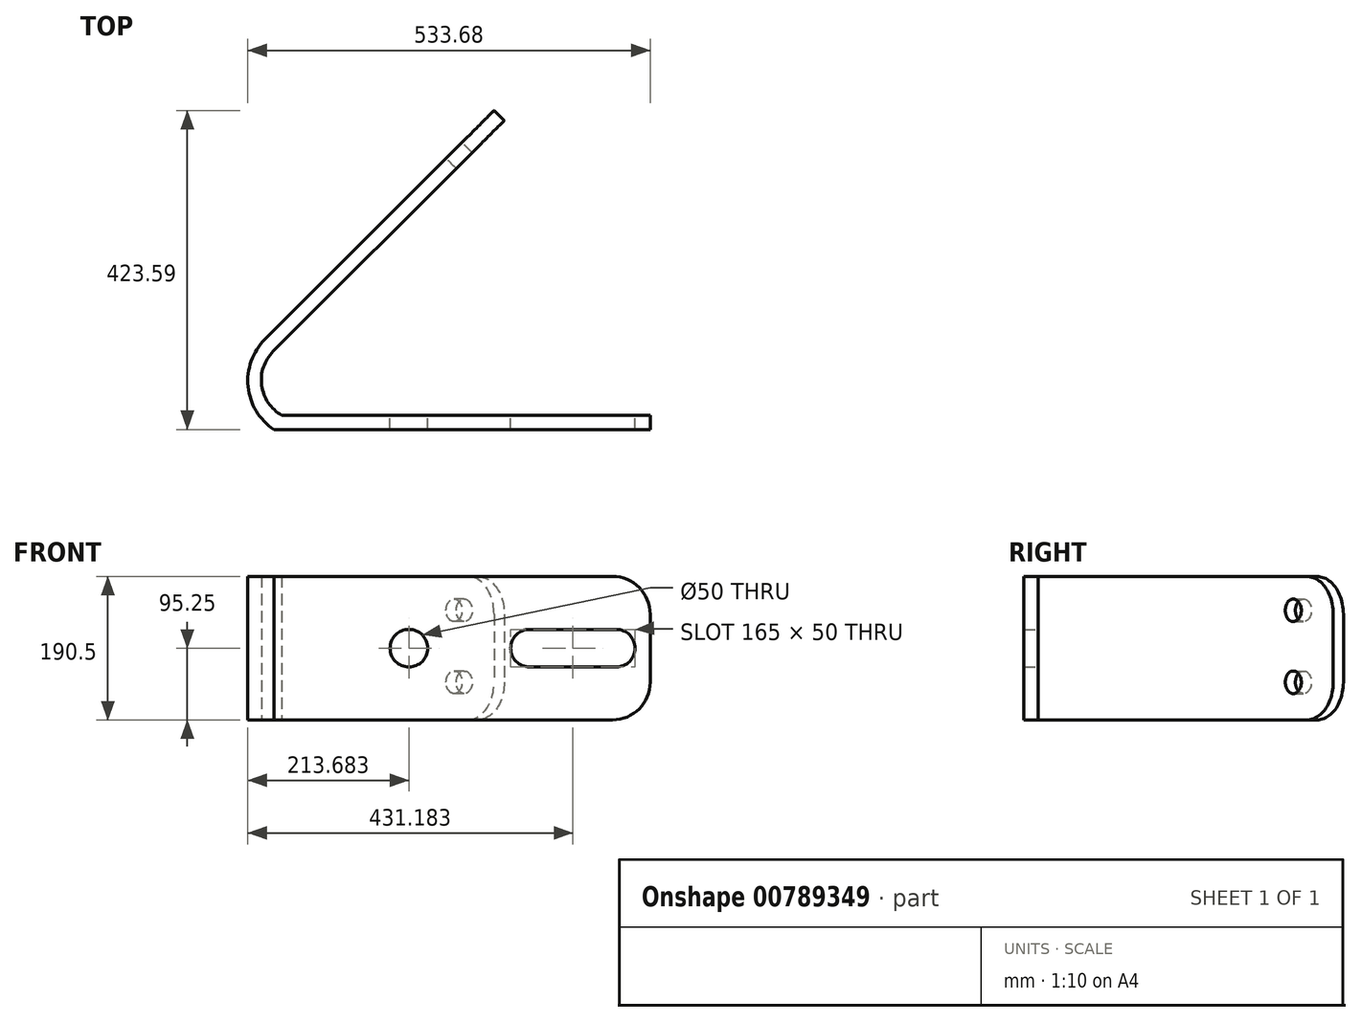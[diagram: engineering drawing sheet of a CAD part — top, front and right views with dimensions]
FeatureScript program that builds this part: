
annotation { "Feature Type Name" : "Feature", "Feature Type Description" : "" }
export const myFeature = defineFeature(function(context is Context, id is Id, definition is map)
    precondition{}
    {
        {
            var Q0;
            Q0=qCreatedBy(makeId("Top.planeOp"),FACE);
            var sketch = newSketch(context, id + "F0", { "sketchPlane" : qUnion([Q0])});
            skLineSegment(sketch, "E0", {"start": v(-480.6, 0) * mm, "end": v(7.87, 0) * mm});
            skPoint(sketch, "E1.start.orphan", {"position": v(-492.13, 223.52) * mm});
            skLineSegment(sketch, "E2", {"start": v(-492.13, 84.75) * mm, "end": v(-185.72, 391.15) * mm});
            skLineSegment(sketch, "E3", {"start": v(-185.72, 391.15) * mm, "end": v(-492.13, 84.75) * mm});
            skLineSegment(sketch, "E4", {"start": v(7.87, 0) * mm, "end": v(7.87, -19) * mm});
            skLineSegment(sketch, "E5", {"start": v(7.87, -19) * mm, "end": v(-491.07, -19) * mm});
            skLineSegment(sketch, "E6", {"start": v(-185.72, 391.15) * mm, "end": v(-199.15, 404.59) * mm});
            skLineSegment(sketch, "E7", {"start": v(-199.15, 404.59) * mm, "end": v(-503.05, 100.7) * mm});
            skArc(sketch, "E8", {"start": v(-503.05, 100.7) * mm, "mid": v(-525.42, 38) * mm, "end": v(-491.07, -19) * mm});
            skPoint(sketch, "E9.orphan", {"position": v(-492.13, 0) * mm});
            skPoint(sketch, "E10.start.orphan", {"position": v(-492.13, 75.02) * mm});
            skArc(sketch, "E11", {"start": v(-492.13, 84.75) * mm, "mid": v(-507.37, 39.52) * mm, "end": v(-480.6, 0) * mm});
            skSolve(sketch);
        }
        {
            var Q0;
            Q0 = qSketchRegion(id + "F0", true);
            extrude(context, id + "F1", {"entities" : qUnion([Q0]), "depth" : 190.5 * mm, "offsetDistance" : 25.4 * mm});
        }
        {
            var Q0;
            Q0=makeQuery(id+"F1.opExtrude","CAP_EDGE",EDGE,{"disambiguationData":[OSD([sQuery(id+"F0.wireOp",EDGE,"E6")])],"isStart":false});
            var Q1;
            Q1=makeQuery(id+"F1.opExtrude","CAP_EDGE",EDGE,{"disambiguationData":[OSD([sQuery(id+"F0.wireOp",EDGE,"E6")])],"isStart":true});
            var Q2;
            Q2=makeQuery(id+"F1.opExtrude","CAP_EDGE",EDGE,{"disambiguationData":[OSD([sQuery(id+"F0.wireOp",EDGE,"E4")])],"isStart":false});
            var Q3;
            Q3=makeQuery(id+"F1.opExtrude","CAP_EDGE",EDGE,{"disambiguationData":[OSD([sQuery(id+"F0.wireOp",EDGE,"E4")])],"isStart":true});
            fillet(context, id + "F2", {"entities" : qUnion([Q0, Q1, Q2, Q3]), "radius" : 50 * mm, "tangentPropagation" : true, "allowEdgeOverflow" : false});
        }
        {
            var Q0;
            Q0=makeQuery(id+"F1.opExtrude","SWEPT_FACE",FACE,{"disambiguationData":[OSD([sQuery(id+"F0.wireOp",EDGE,"E7")])]});
            var sketch = newSketch(context, id + "F3", { "sketchPlane" : qUnion([Q0])});
            skLineSegment(sketch, "E12", {"start": v(-145.26, 0) * mm, "end": v(-70.26, 0) * mm, "construction": true});
            skLineSegment(sketch, "E13", {"start": v(-145.26, 0) * mm, "end": v(-145.26, 50) * mm, "construction": true});
            skCircle(sketch, "E14", {"center": v(-70.26, 50) * mm, "radius": 15 * mm});
            skLineSegment(sketch, "E15", {"start": v(-55.26, 145.5) * mm, "end": v(-70.26, 145.5) * mm, "construction": true});
            skCircle(sketch, "E16", {"center": v(-70.26, 145.5) * mm, "radius": 15 * mm, "construction": true});
            skCircle(sketch, "E17", {"center": v(-70.26, 145.5) * mm, "radius": 15 * mm});
            skSolve(sketch);
        }
        {
            var Q0;
            Q0=makeQuery(id+"F3.imprint","IMPRINT",FACE,{"disambiguationData":[TD([[makeQuery(id+"F3.imprint","IMPRINT",EDGE,{"derivedFrom":sQuery(id+"F3.wireOp",EDGE,"E17")}),1.0]])]});
            var Q1;
            Q1=makeQuery(id+"F3.imprint","IMPRINT",FACE,{"disambiguationData":[TD([[makeQuery(id+"F3.imprint","IMPRINT",EDGE,{"derivedFrom":sQuery(id+"F3.wireOp",EDGE,"E14")}),1.0]])]});
            extrude(context, id + "F4", {"entities" : qUnion([Q0, Q1]), "operationType" : NewBodyOperationType.REMOVE, "oppositeDirection" : true, "depth" : 101.6 * mm, "offsetDistance" : 25.4 * mm});
        }
        {
            var Q0;
            Q0=makeQuery(id+"F1.opExtrude","SWEPT_FACE",FACE,{"disambiguationData":[OSD([sQuery(id+"F0.wireOp",EDGE,"E0")])]});
            var sketch = newSketch(context, id + "F5", { "sketchPlane" : qUnion([Q0])});
            skLineSegment(sketch, "E18", {"start": v(-7.87, 95.25) * mm, "end": v(312.13, 95.25) * mm, "construction": true});
            skCircle(sketch, "E19", {"center": v(312.13, 95.25) * mm, "radius": 25 * mm});
            skArc(sketch, "E20", {"start": v(37.13, 120.25) * mm, "mid": v(12.13, 95.25) * mm, "end": v(37.13, 70.25) * mm});
            skArc(sketch, "E21", {"start": v(152.13, 70.25) * mm, "mid": v(177.13, 95.25) * mm, "end": v(152.13, 120.25) * mm});
            skLineSegment(sketch, "E22", {"start": v(152.13, 70.25) * mm, "end": v(37.13, 70.25) * mm});
            skLineSegment(sketch, "E23", {"start": v(37.13, 120.25) * mm, "end": v(152.13, 120.25) * mm});
            skSolve(sketch);
        }
        {
            var Q0;
            Q0 = qSketchRegion(id + "F5", true);
            extrude(context, id + "F6", {"entities" : qUnion([Q0]), "operationType" : NewBodyOperationType.REMOVE, "oppositeDirection" : true, "depth" : 101.6 * mm, "offsetDistance" : 25.4 * mm});
        }
    });
